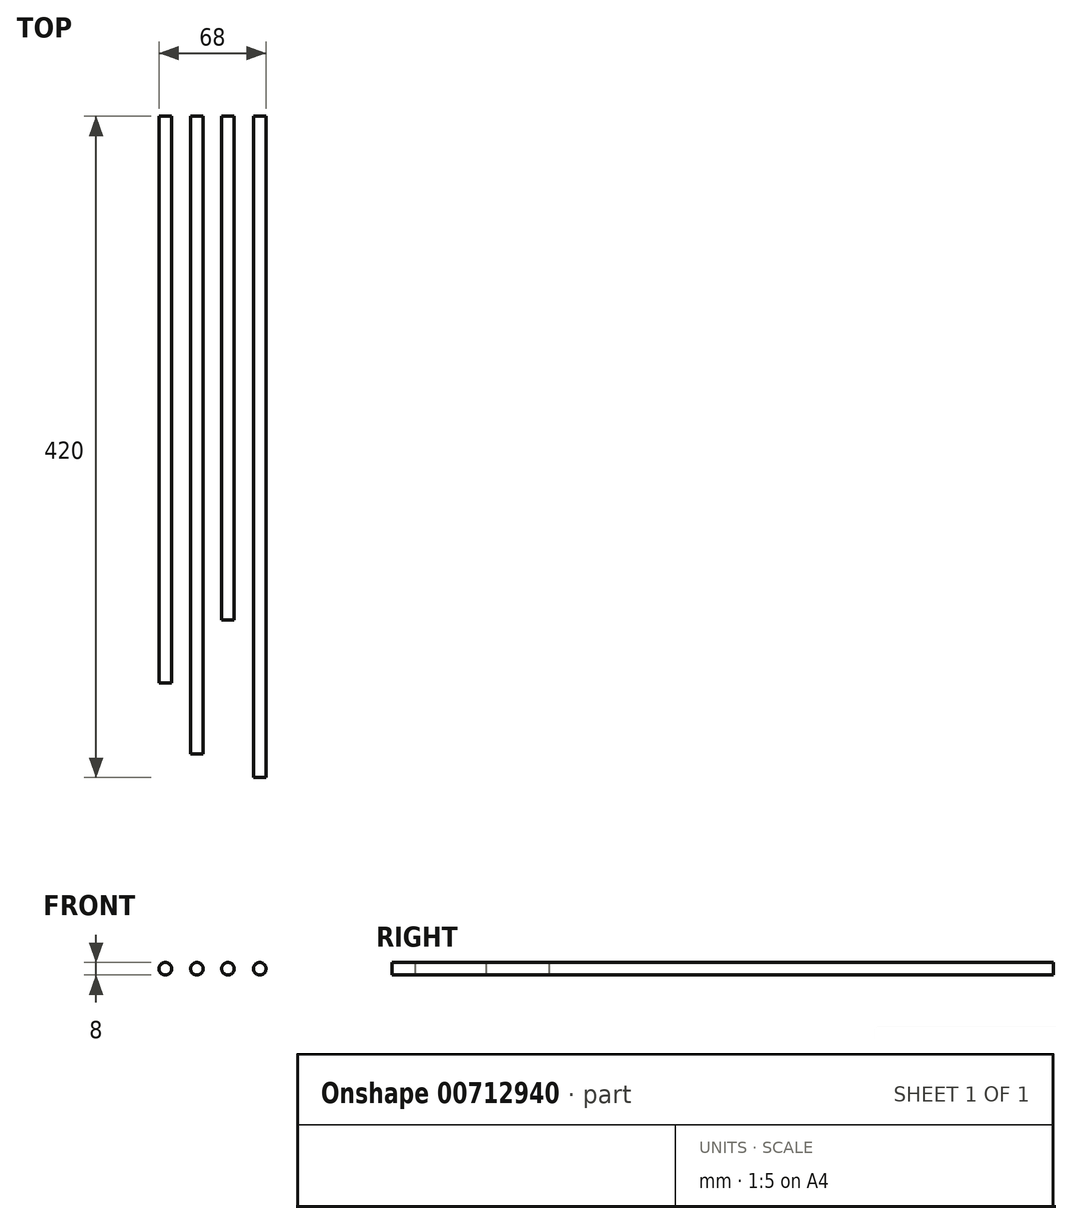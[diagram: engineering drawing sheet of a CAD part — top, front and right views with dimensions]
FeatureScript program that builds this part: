
annotation { "Feature Type Name" : "Feature", "Feature Type Description" : "" }
export const myFeature = defineFeature(function(context is Context, id is Id, definition is map)
    precondition{}
    {
        {
            var Q0;
            Q0=qCreatedBy(makeId("Front.planeOp"),FACE);
            var sketch = newSketch(context, id + "F0", { "sketchPlane" : qUnion([Q0])});
            skCircle(sketch, "E0", {"center": v(0, 0) * mm, "radius": 4 * mm});
            skSolve(sketch);
        }
        {
            var Q0;
            Q0 = qSketchRegion(id + "F0", true);
            extrude(context, id + "F1", {"entities" : qUnion([Q0]), "depth" : 360 * mm, "offsetDistance" : 25 * mm});
        }
        {
            var Q0;
            Q0=qCreatedBy(makeId("Front.planeOp"),FACE);
            var sketch = newSketch(context, id + "F2", { "sketchPlane" : qUnion([Q0])});
            skCircle(sketch, "E1", {"center": v(20.01, 0) * mm, "radius": 4 * mm});
            skSolve(sketch);
        }
        {
            var Q0;
            Q0=makeQuery(id+"F2.imprint","IMPRINT",FACE,{"disambiguationData":[TD([[makeQuery(id+"F2.imprint","IMPRINT",EDGE,{"derivedFrom":sQuery(id+"F2.wireOp",EDGE,"E1")}),1.0]])]});
            extrude(context, id + "F3", {"entities" : qUnion([Q0]), "depth" : 405 * mm, "offsetDistance" : 25 * mm});
        }
        {
            var Q0;
            Q0=qCreatedBy(makeId("Front.planeOp"),FACE);
            var sketch = newSketch(context, id + "F4", { "sketchPlane" : qUnion([Q0])});
            skCircle(sketch, "E2", {"center": v(39.72, 0) * mm, "radius": 4 * mm});
            skSolve(sketch);
        }
        {
            var Q0;
            Q0=makeQuery(id+"F4.imprint","IMPRINT",FACE,{"disambiguationData":[TD([[makeQuery(id+"F4.imprint","IMPRINT",EDGE,{"derivedFrom":sQuery(id+"F4.wireOp",EDGE,"E2")}),1.0]])]});
            extrude(context, id + "F5", {"entities" : qUnion([Q0]), "depth" : 320 * mm, "offsetDistance" : 25 * mm});
        }
        {
            var Q0;
            Q0=qCreatedBy(makeId("Front.planeOp"), FACE);
            var sketch = newSketch(context, id + "F6", { "sketchPlane" : qUnion([Q0])});
            skCircle(sketch, "E3", {"center": v(60, 0) * mm, "radius": 4 * mm});
            skSolve(sketch);
        }
        {
            var Q0;
            Q0 = qSketchRegion(id + "F6", true);
            extrude(context, id + "F7", {"entities" : qUnion([Q0]), "domain" : OperationDomain.MODEL, "flatOperationType" : FlatOperationType.REMOVE, "depth" : 420 * mm, "offsetDistance" : 25 * mm});
        }
    });
